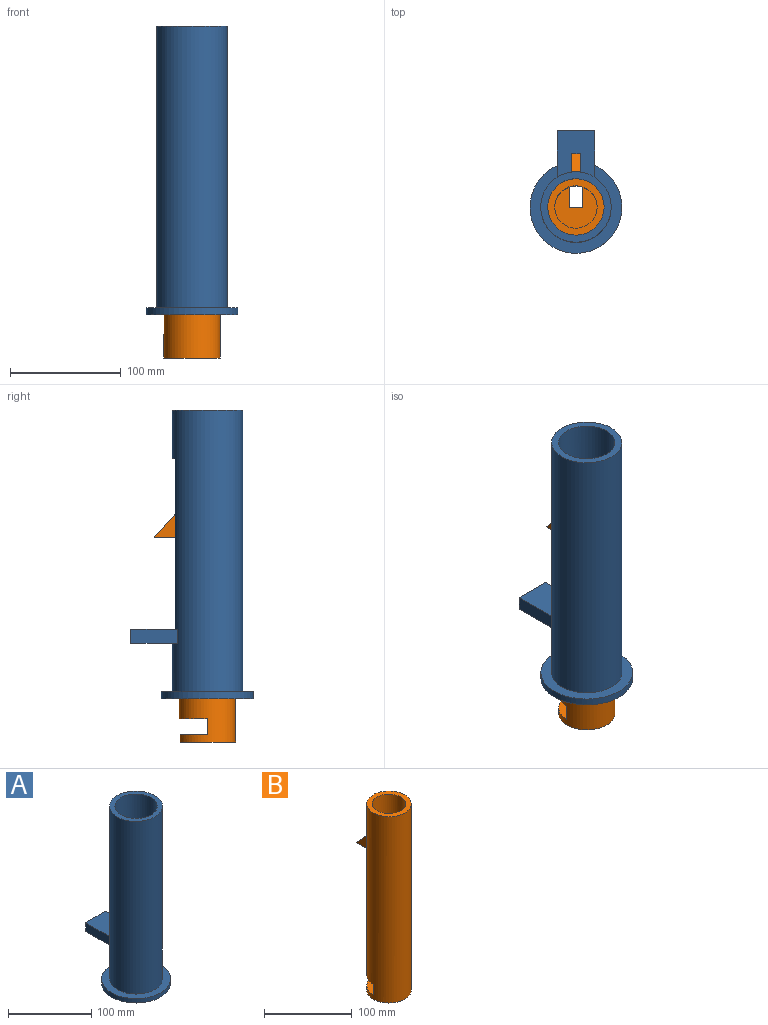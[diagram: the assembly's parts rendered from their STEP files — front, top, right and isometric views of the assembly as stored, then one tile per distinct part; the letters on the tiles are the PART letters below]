
ASSEMBLY  parts=2 mates=1
PART A: 18 faces, bbox 82.8x110.5x260.4 mm
  f0: cylinder r=31.75mm len=254mm, axis (0,0,-1), area 46205mm2, adj f2,f3,f4,f6,f11,f12,f13,f14
  f1: cylinder r=25.4mm len=254mm, axis (0,0,1), area 36112.8mm2, adj f2,f3,f4,f5,f6,f7
  f2: plane 63.5x63.5mm, normal (0,0,1), area 1140.1mm2, adj f0,f1
  f3: plane 25.4x9.75mm, normal (0,0,-1), area 167.2mm2, adj f0,f1,f4,f6
  f4: plane 166.31x7.1mm, normal (1,0,0), area 1148.5mm2, adj f0,f1,f3,f5,f15,f16
  f5: plane 25.4x4.52mm, normal (0,0,1), area 56.4mm2, adj f1,f4,f6,f15
  f6: plane 166.31x7.1mm, normal (-1,0,0), area 1148.5mm2, adj f0,f1,f3,f5,f15,f16
  f7: plane 50.8x50.8mm, normal (0,0,1), area 15mm2, adj f1,f8
  f8: cylinder r=25.31mm len=50.61mm, axis (0,0,1), area 1009.7mm2, adj f7,f10
  f9: cylinder r=41.41mm len=82.81mm, axis (0,0,1), area 1652.1mm2, adj f10,f11
  f10: plane 82.81x82.81mm, normal (0,0,-1), area 3374.5mm2, adj f8,f9
  f11: plane 82.81x82.81mm, normal (0,0,1), area 2219.4mm2, adj f0,f9
  f12: plane 42.18x12.7mm, normal (1,0,0), area 535.7mm2, adj f0,f14,f16,f17
  f13: plane 42.18x12.7mm, normal (-1,0,0), area 535.7mm2, adj f0,f14,f16,f17
  f14: plane 42.18x33.73mm, normal (0,0,-1), area 1311.9mm2, adj f0,f12,f13,f17
  f15: plane 25.4x12.7mm, normal (0,-1,0), area 322.6mm2, adj f4,f5,f6,f16
  f16: plane 42.56x33.73mm, normal (0,0,1), area 1422.7mm2, adj f0,f4,f6,f12,f13,f15,f17
  f17: plane 33.73x12.7mm, normal (0,1,0), area 428.3mm2, adj f12,f13,f14,f16
PART B: 17 faces, bbox 50.8x73.4x260.4 mm
  f0: plane 50.8x43.76mm, normal (0,0,1), area 1276.6mm2, adj f3,f4,f10,f12,f13,f14,f15,f16
  f1: plane 50.8x50.03mm, normal (0,0,-1), area 1715.5mm2, adj f3,f4,f14,f15,f16
  f2: plane 25.4x22.94mm, normal (-1,0,0), area 291.3mm2, adj f3,f7,f9
  f3: cylinder r=25.4mm len=260.35mm, axis (0,0,-1), area 39888.6mm2, adj f0,f1,f2,f4,f5,f6,f7,f8
  f4: cylinder r=25.4mm len=24.63mm, axis (0,0,-1), area 213.6mm2, adj f0,f1,f3,f14
  f5: plane 50.8x50.8mm, normal (0,0,1), area 877.7mm2, adj f3,f10
  f6: plane 25.4x22.94mm, normal (1,0,0), area 291.3mm2, adj f3,f7,f9
  f7: plane 22.94x7.83mm, normal (0,0,-1), area 177.9mm2, adj f2,f3,f6,f9
  f8: plane 7.83x0.3mm, normal (0,0,-1), area 1.6mm2, adj f3,f9
  f9: plane 25.4x22.94mm, normal (0,0.74,0.67), area 267.8mm2, adj f2,f6,f7,f8
  f10: cylinder r=19.13mm len=254mm, axis (0,0,-1), area 29642.6mm2, adj f0,f5,f11,f12,f13
  f11: plane 50.8x25.4mm, normal (0,0,-1), area 438.9mm2, adj f3,f10,f12,f13
  f12: plane 14.65x6.27mm, normal (0,1,0), area 91.9mm2, adj f0,f3,f10,f11
  f13: plane 14.65x6.27mm, normal (0,1,0), area 91.9mm2, adj f0,f3,f10,f11
  f14: plane 24.63x6.35mm, normal (-1,0,0), area 156.4mm2, adj f0,f1,f4,f16
  f15: plane 24.63x6.35mm, normal (1,0,0), area 156.4mm2, adj f0,f1,f3,f16
  f16: plane 12.38x6.35mm, normal (0,1,0), area 78.6mm2, adj f0,f1,f14,f15
PLACE A t=(-62.25,61.87,22.89)mm fixed
PLACE B t=(-62.25,61.87,-16.04)mm
MATE slider B.f3 <-> A.f1  axis (0,0,-1) through (-62.25,61.87,107.78)mm
